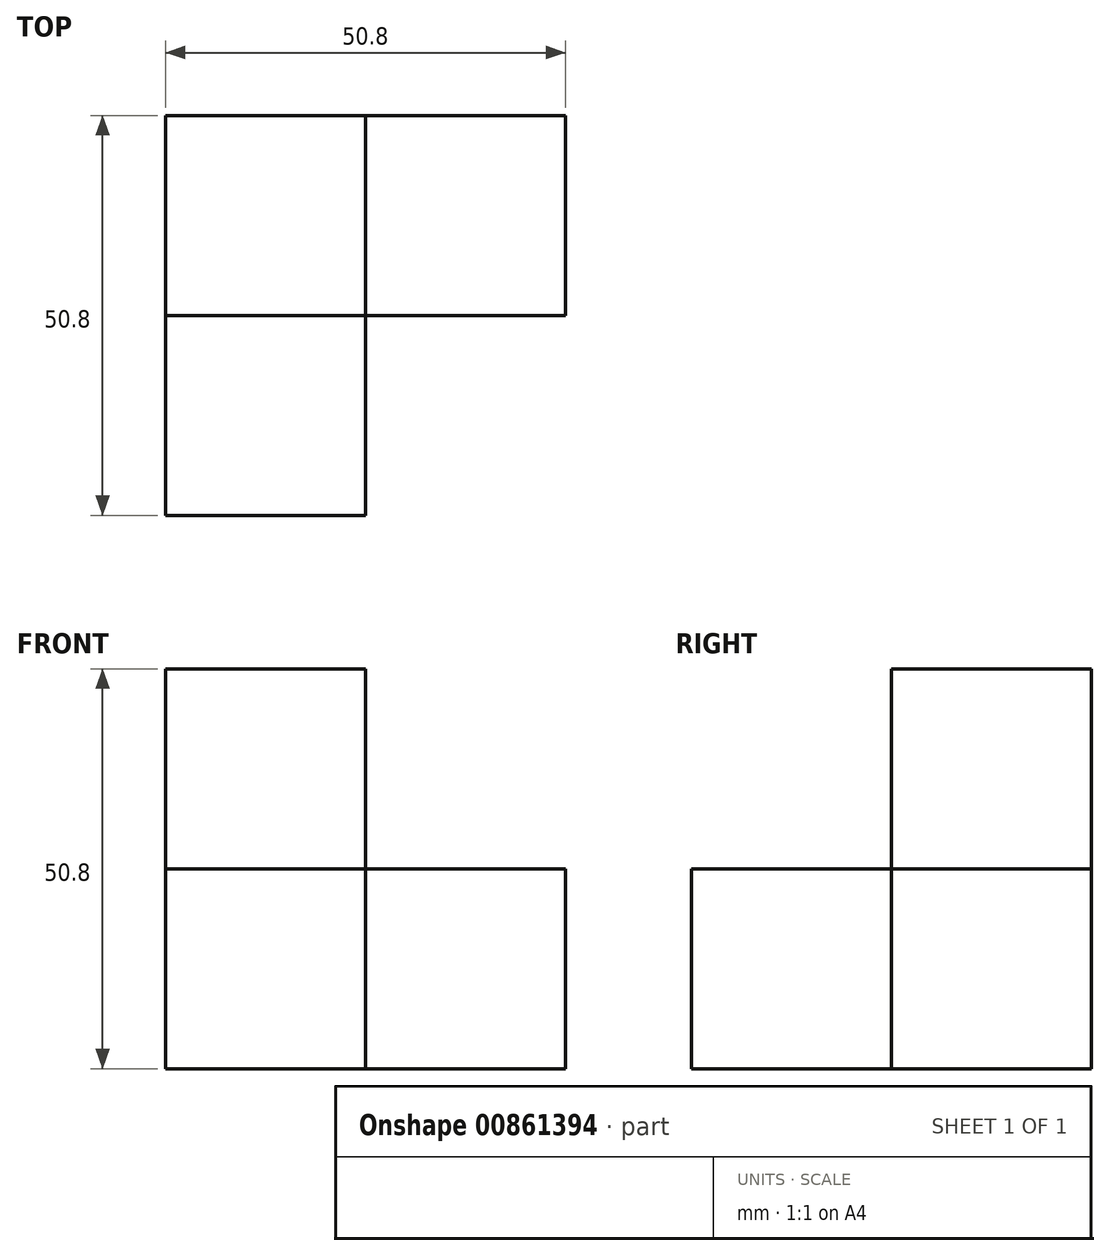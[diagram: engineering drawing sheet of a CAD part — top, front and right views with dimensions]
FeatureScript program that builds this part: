
annotation { "Feature Type Name" : "Feature", "Feature Type Description" : "" }
export const myFeature = defineFeature(function(context is Context, id is Id, definition is map)
    precondition{}
    {
        {
            var Q0;
            Q0=qCreatedBy(makeId("Top.planeOp"),FACE);
            var sketch = newSketch(context, id + "F0", { "sketchPlane" : qUnion([Q0])});
            skLineSegment(sketch, "E0.bottom", {"start": v(25.4, -12.7) * mm, "end": v(0, -12.7) * mm});
            skLineSegment(sketch, "E0.top", {"start": v(25.4, 12.7) * mm, "end": v(-25.4, 12.7) * mm});
            skLineSegment(sketch, "E0.left", {"start": v(25.4, -12.7) * mm, "end": v(25.4, 12.7) * mm});
            skLineSegment(sketch, "E0.right", {"start": v(-25.4, -12.7) * mm, "end": v(-25.4, 12.7) * mm});
            skPoint(sketch, "E0.middle", {"position": v(0, 0) * mm});
            skLineSegment(sketch, "E1.top", {"start": v(-25.4, -38.1) * mm, "end": v(0, -38.1) * mm});
            skLineSegment(sketch, "E1.left", {"start": v(-25.4, -12.7) * mm, "end": v(-25.4, -38.1) * mm});
            skLineSegment(sketch, "E1.right", {"start": v(0, -12.7) * mm, "end": v(0, -38.1) * mm});
            skSolve(sketch);
        }
        {
            var Q0;
            Q0 = qSketchRegion(id + "F0", true);
            extrude(context, id + "F1", {"entities" : qUnion([Q0]), "depth" : 25.4 * mm, "offsetDistance" : 25.4 * mm});
        }
        {
            var Q0;
            Q0=makeQuery(id+"F1.opExtrude","CAP_FACE",FACE,{"disambiguationData":[OSD([sQuery(id+"F0.wireOp",EDGE,"E0.bottom"),sQuery(id+"F0.wireOp",EDGE,"E0.top"),sQuery(id+"F0.wireOp",EDGE,"E0.left"),sQuery(id+"F0.wireOp",EDGE,"E0.right"),sQuery(id+"F0.wireOp",EDGE,"E1.top"),sQuery(id+"F0.wireOp",EDGE,"E1.left"),sQuery(id+"F0.wireOp",EDGE,"E1.right")])],"isStart":false});
            var sketch = newSketch(context, id + "F2", { "sketchPlane" : qUnion([Q0])});
            skLineSegment(sketch, "E2.bottom", {"start": v(-25.4, 12.7) * mm, "end": v(0, 12.7) * mm});
            skLineSegment(sketch, "E2.top", {"start": v(-25.4, -12.7) * mm, "end": v(0, -12.7) * mm});
            skLineSegment(sketch, "E2.left", {"start": v(-25.4, 12.7) * mm, "end": v(-25.4, -12.7) * mm});
            skLineSegment(sketch, "E2.right", {"start": v(0, 12.7) * mm, "end": v(0, -12.7) * mm});
            skSolve(sketch);
        }
        {
            var Q0;
            Q0 = qSketchRegion(id + "F2", true);
            extrude(context, id + "F3", {"entities" : qUnion([Q0]), "operationType" : NewBodyOperationType.ADD, "depth" : 25.4 * mm, "offsetDistance" : 25.4 * mm});
        }
    });
